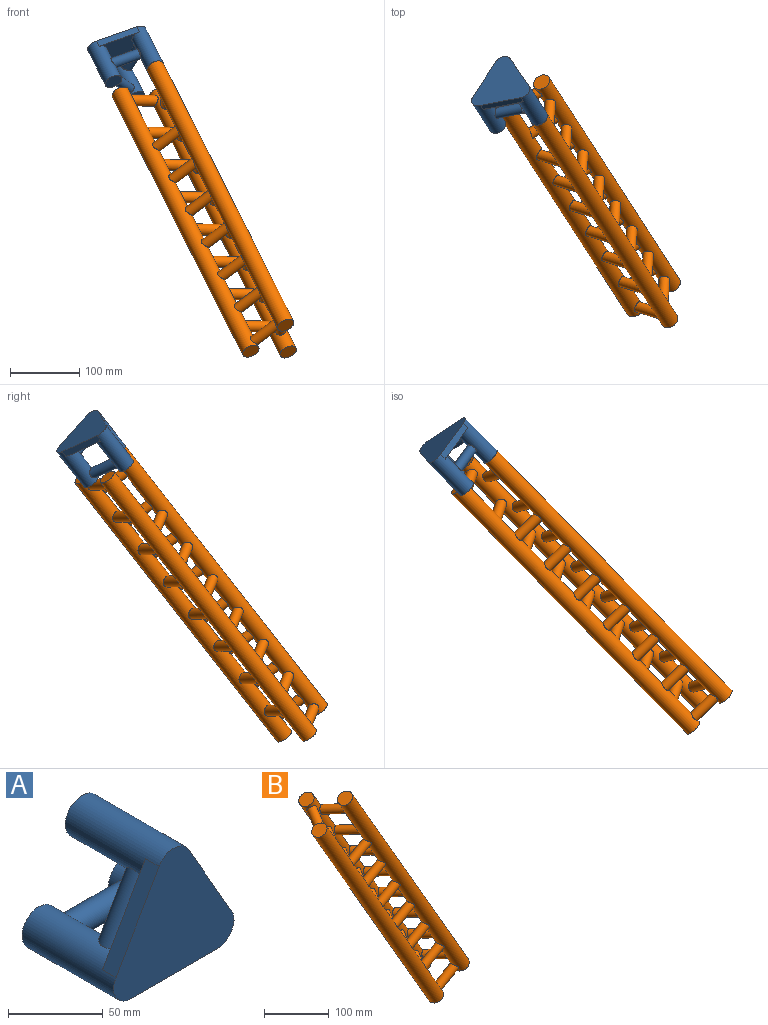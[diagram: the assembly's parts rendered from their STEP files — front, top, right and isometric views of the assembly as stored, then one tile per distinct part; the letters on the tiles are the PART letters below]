
ASSEMBLY  parts=2 mates=1
PART A: 15 faces, bbox 90.1x68.6x81.4 mm
  f0: cylinder r=12.7mm len=68.58mm, axis (0,1,0), area 4570.6mm2, adj f1,f2,f3,f10,f11,f12,f14
  f1: plane 25.4x25.4mm, normal (0,1,0), area 506.7mm2, adj f0
  f2: cylinder r=7.62mm len=44.21mm, axis (-0.5,0,0.87), area 1925.1mm2, adj f0,f4
  f3: cylinder r=7.62mm len=44.34mm, axis (-1,0,0), area 1997.5mm2, adj f0,f7
  f4: cone r=7.62mm half-angle=60deg, axis (0.5,0,-0.87), area 80.7mm2, adj f2,f5
  f5: cylinder r=12.7mm len=68.58mm, axis (0,1,0), area 4609mm2, adj f4,f6,f9,f10,f12,f13,f14
  f6: cylinder r=7.95mm len=46.79mm, axis (0.5,0,0.87), area 2096.4mm2, adj f5,f7
  f7: cylinder r=12.7mm len=68.58mm, axis (0,1,0), area 4535.7mm2, adj f3,f6,f8,f10,f11,f13,f14
  f8: plane 25.4x25.4mm, normal (0,1,0), area 506.7mm2, adj f7
  f9: plane 25.4x25.4mm, normal (0,1,0), area 506.7mm2, adj f5
  f10: plane 85.49x75.04mm, normal (0,1,0), area 3255.1mm2, adj f0,f5,f7,f11,f12,f13
  f11: plane 63.89x10.16mm, normal (0,0,-1), area 649.1mm2, adj f0,f7,f10,f14
  f12: plane 54.22x31.15mm, normal (0.87,0,0.5), area 635.3mm2, adj f0,f5,f10,f14
  f13: plane 55.8x32.21mm, normal (-0.87,0,0.5), area 654.6mm2, adj f5,f7,f10,f14
  f14: plane 90.05x81.39mm, normal (0,-1,0), area 4775.2mm2, adj f0,f5,f7,f11,f12,f13
PART B: 40 faces, bbox 332x81.4x485 mm
  f0: cylinder r=7.62mm len=46.02mm, axis (0.87,0,0.5), area 1998mm2, adj f4,f6
  f1: cylinder r=12.7mm len=452.64mm, axis (-0.5,0,0.87), area 37932.2mm2, adj f2,f5,f8,f10,f12,f15,f17,f19
  f2: cone r=7.62mm half-angle=60deg, axis (0.43,-0.87,0.25), area 80.9mm2, adj f1,f3
  f3: cylinder r=7.62mm len=44.21mm, axis (0.43,-0.87,0.25), area 1922.7mm2, adj f2,f4
  f4: cylinder r=12.7mm len=452.64mm, axis (-0.5,0,0.87), area 37437.2mm2, adj f0,f3,f7,f9,f11,f13,f14,f18
  f5: cylinder r=7.95mm len=46.79mm, axis (-0.43,-0.87,-0.25), area 2096.6mm2, adj f1,f6
  f6: cylinder r=12.7mm len=452.64mm, axis (-0.5,0,0.87), area 37492.1mm2, adj f0,f5,f7,f10,f11,f15,f16,f18
  f7: cylinder r=7.62mm len=46.02mm, axis (0.87,0,0.5), area 1998mm2, adj f4,f6
  f8: cone r=7.62mm half-angle=60deg, axis (0.43,-0.87,0.25), area 80.9mm2, adj f1,f9
  f9: cylinder r=7.62mm len=44.21mm, axis (0.43,-0.87,0.25), area 1922.7mm2, adj f4,f8
  f10: cylinder r=7.95mm len=46.79mm, axis (-0.43,-0.87,-0.25), area 2096.6mm2, adj f1,f6
  f11: cylinder r=7.62mm len=46.02mm, axis (0.87,0,0.5), area 1998mm2, adj f4,f6
  f12: cone r=7.62mm half-angle=60deg, axis (0.43,-0.87,0.25), area 80.9mm2, adj f1,f13
  f13: cylinder r=7.62mm len=44.21mm, axis (0.43,-0.87,0.25), area 1922.7mm2, adj f4,f12
  f14: plane 25.4x22mm, normal (0.5,0,-0.87), area 506.7mm2, adj f4
  f15: cylinder r=7.95mm len=46.79mm, axis (-0.43,-0.87,-0.25), area 2096.6mm2, adj f1,f6
  f16: plane 25.4x22mm, normal (0.5,0,-0.87), area 506.7mm2, adj f6
  f17: plane 25.4x22mm, normal (0.5,0,-0.87), area 506.7mm2, adj f1
  f18: cylinder r=7.62mm len=46.02mm, axis (0.87,0,0.5), area 1998mm2, adj f4,f6
  f19: cone r=7.62mm half-angle=60deg, axis (0.43,-0.87,0.25), area 80.9mm2, adj f1,f20
  f20: cylinder r=7.62mm len=44.21mm, axis (0.43,-0.87,0.25), area 1922.7mm2, adj f4,f19
  f21: cylinder r=7.95mm len=46.79mm, axis (-0.43,-0.87,-0.25), area 2096.6mm2, adj f1,f6
  f22: cylinder r=7.62mm len=46.02mm, axis (0.87,0,0.5), area 1998mm2, adj f4,f6
  f23: cone r=7.62mm half-angle=60deg, axis (0.43,-0.87,0.25), area 80.9mm2, adj f1,f24
  f24: cylinder r=7.62mm len=44.21mm, axis (0.43,-0.87,0.25), area 1922.7mm2, adj f4,f23
  f25: cylinder r=7.95mm len=46.79mm, axis (-0.43,-0.87,-0.25), area 2096.6mm2, adj f1,f6
  f26: cylinder r=7.62mm len=46.02mm, axis (0.87,0,0.5), area 1998mm2, adj f4,f6
  f27: cone r=7.62mm half-angle=60deg, axis (0.43,-0.87,0.25), area 80.9mm2, adj f1,f28
  f28: cylinder r=7.62mm len=44.21mm, axis (0.43,-0.87,0.25), area 1922.7mm2, adj f4,f27
  f29: cylinder r=7.95mm len=46.79mm, axis (-0.43,-0.87,-0.25), area 2096.6mm2, adj f1,f6
  f30: cone r=7.62mm half-angle=60deg, axis (0.43,-0.87,0.25), area 80.9mm2, adj f1,f31
  f31: cylinder r=7.62mm len=44.21mm, axis (0.43,-0.87,0.25), area 1922.7mm2, adj f4,f30
  f32: plane 25.4x22mm, normal (-0.5,0,0.87), area 506.7mm2, adj f4
  f33: cylinder r=7.95mm len=46.79mm, axis (-0.43,-0.87,-0.25), area 2096.6mm2, adj f1,f6
  f34: plane 25.4x22mm, normal (-0.5,0,0.87), area 506.7mm2, adj f6
  f35: plane 25.4x22mm, normal (-0.5,0,0.87), area 506.7mm2, adj f1
  f36: cylinder r=7.62mm len=46.02mm, axis (0.87,0,0.5), area 1998mm2, adj f4,f6
  f37: cone r=7.62mm half-angle=60deg, axis (0.43,-0.87,0.25), area 80.9mm2, adj f1,f38
  f38: cylinder r=7.62mm len=44.21mm, axis (0.43,-0.87,0.25), area 1922.7mm2, adj f4,f37
  f39: cylinder r=7.95mm len=46.79mm, axis (-0.43,-0.87,-0.25), area 2096.6mm2, adj f1,f6
PLACE A rot(axis=(-0.37,0.32,-0.87),138.6deg) t=(-665.86,-354.04,-128.43)mm
PLACE B rot(axis=(-0.59,-0.06,-0.81),38.5deg) t=(-494.01,-578.22,-277.16)mm
MATE fastened A.f5 <-> B.f4  axis (0.37,-0.57,-0.73) through (-639.7,-358.72,-101.13)mm
